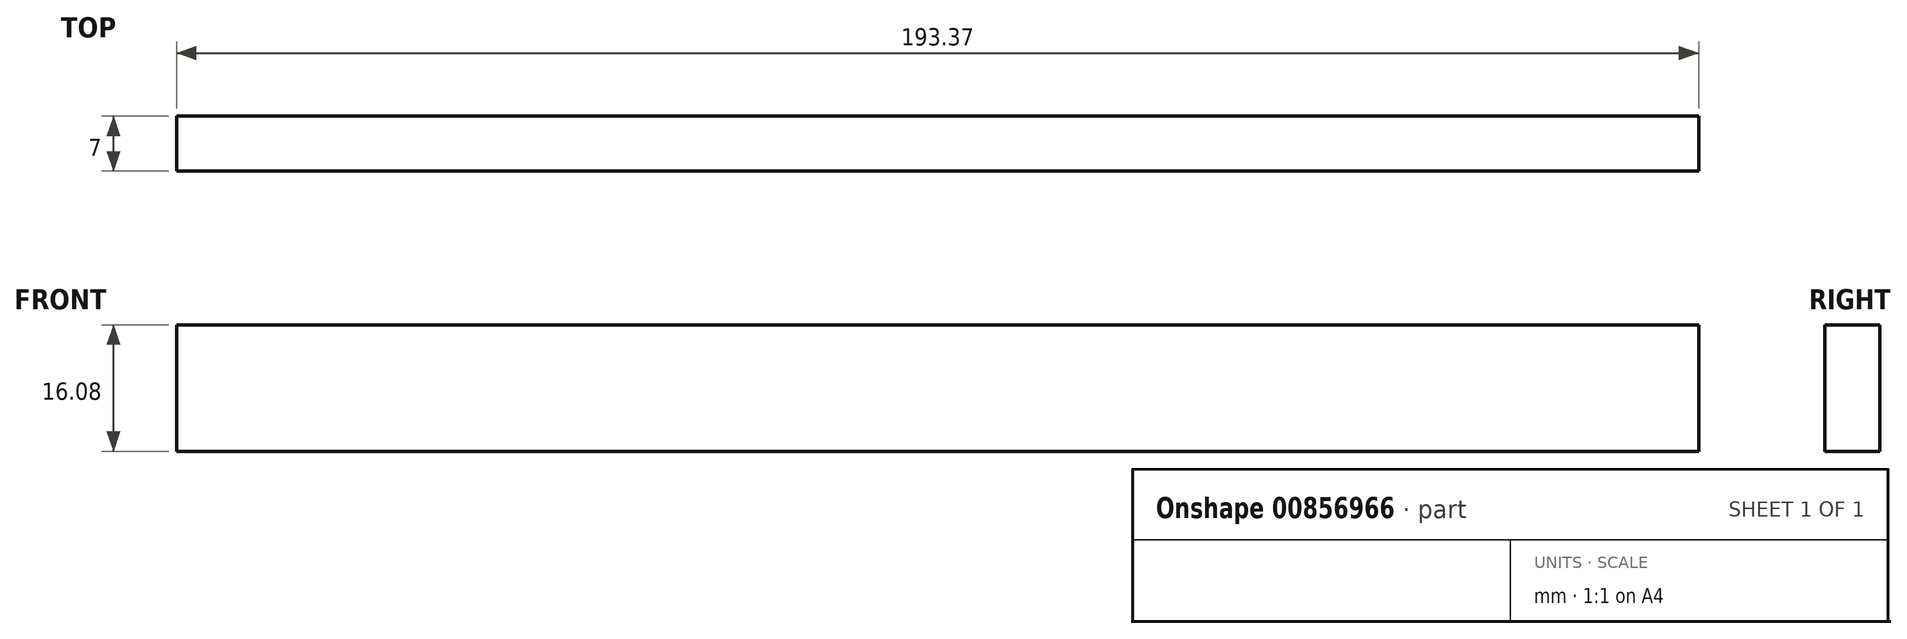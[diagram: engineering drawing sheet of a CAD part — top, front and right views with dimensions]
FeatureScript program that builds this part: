
annotation { "Feature Type Name" : "Feature", "Feature Type Description" : "" }
export const myFeature = defineFeature(function(context is Context, id is Id, definition is map)
    precondition{}
    {
        {
            var Q0;
            Q0=qCreatedBy(makeId("Front.planeOp"),FACE);
            var sketch = newSketch(context, id + "F0", { "sketchPlane" : qUnion([Q0])});
            skLineSegment(sketch, "E0.bottom", {"start": v(-125.92, 60.33) * mm, "end": v(67.45, 60.33) * mm});
            skLineSegment(sketch, "E0.top", {"start": v(-125.92, 76.4) * mm, "end": v(67.45, 76.4) * mm});
            skLineSegment(sketch, "E0.left", {"start": v(-125.92, 60.33) * mm, "end": v(-125.92, 76.4) * mm});
            skLineSegment(sketch, "E0.right", {"start": v(67.45, 60.33) * mm, "end": v(67.45, 76.4) * mm});
            skSolve(sketch);
        }
        {
            var Q0;
            Q0=makeQuery(id+"F0.imprint","IMPRINT",FACE,{"disambiguationData":[TD([[makeQuery(id+"F0.imprint","IMPRINT",EDGE,{"derivedFrom":sQuery(id+"F0.wireOp",EDGE,"E0.bottom")}),1.0]])]});
            extrude(context, id + "F1", {"entities" : qUnion([Q0]), "depth" : 7 * mm, "offsetDistance" : 25 * mm});
        }
    });
